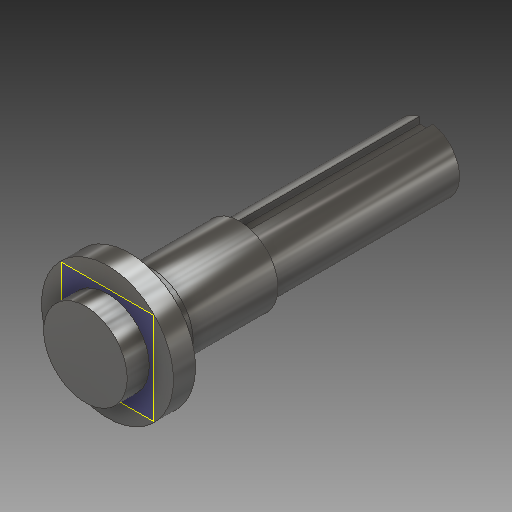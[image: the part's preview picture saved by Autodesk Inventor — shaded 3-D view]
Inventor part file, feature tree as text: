
AUTODESK INVENTOR PART (.ipt)
format: ipt  version: 2019 (Build 230136000, 136)  size: 157,184 bytes
history: native  units: in
note: dims shown in document units (in); Inventor stores cm internally (conversion verified against a paired STEP export)
features: sketch x5, other x3, plane x1
ambient origin geometry x8: Origin, YZ Plane, XZ Plane, XY Plane, X Axis, Y Axis, Z Axis, Center Point
bodies: Solid1 (feature_tree)
feature tree (9):
  other  "project handle part(1).ipt"
  other  "Solid1::project handle part(1).ipt"
  other  "TaggingFeature1"
  sketch  "Sketch1"  dims[d0=0.3937in]
  sketch  "Sketch2"
  sketch  "Sketch3"
  sketch  "Sketch4"
  sketch  "Sketch5"
  plane  "Work Plane1"
